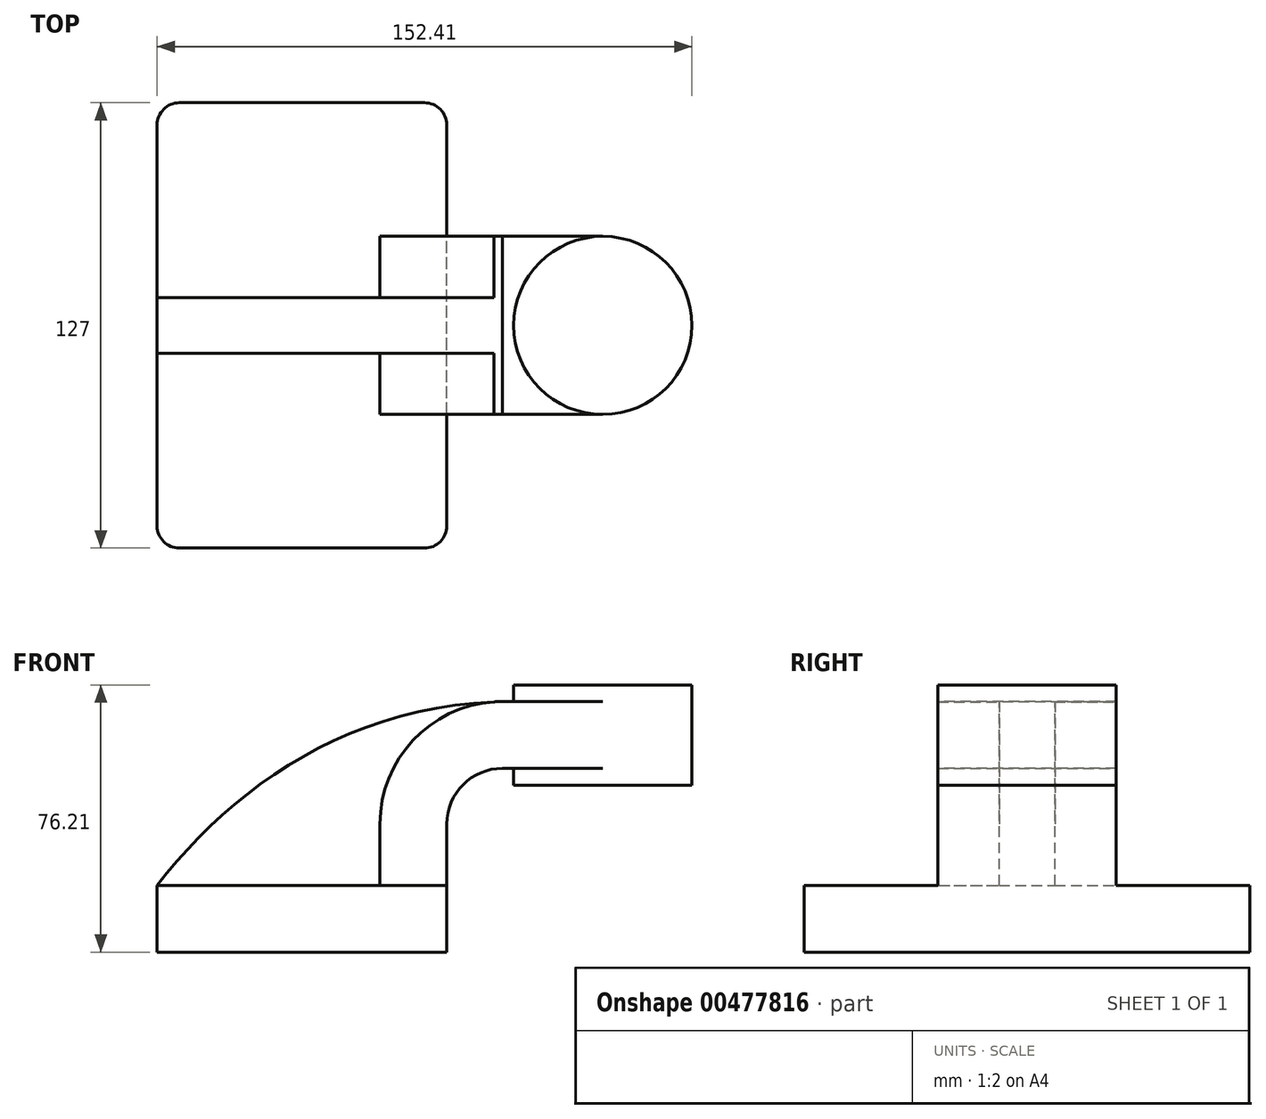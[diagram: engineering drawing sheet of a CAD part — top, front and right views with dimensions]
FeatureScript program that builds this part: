
annotation { "Feature Type Name" : "Feature", "Feature Type Description" : "" }
export const myFeature = defineFeature(function(context is Context, id is Id, definition is map)
    precondition{}
    {
        {
            var Q0;
            Q0=qCreatedBy(makeId("Front.planeOp"),FACE);
            var sketch = newSketch(context, id + "F0", { "sketchPlane" : qUnion([Q0])});
            skLineSegment(sketch, "E0.bottom", {"start": v(41.27, 9.53) * mm, "end": v(-41.27, 9.53) * mm});
            skLineSegment(sketch, "E0.top", {"start": v(41.28, -9.52) * mm, "end": v(-41.27, -9.52) * mm});
            skLineSegment(sketch, "E0.left", {"start": v(41.28, 9.53) * mm, "end": v(41.28, -9.52) * mm});
            skLineSegment(sketch, "E0.right", {"start": v(-41.27, 9.53) * mm, "end": v(-41.27, -9.52) * mm});
            skPoint(sketch, "E0.middle", {"position": v(0, 0) * mm});
            skLineSegment(sketch, "E1.bottom", {"start": v(60.32, 38.1) * mm, "end": v(111.12, 38.1) * mm});
            skLineSegment(sketch, "E1.top", {"start": v(60.32, 66.68) * mm, "end": v(111.12, 66.68) * mm});
            skLineSegment(sketch, "E1.left", {"start": v(60.32, 38.1) * mm, "end": v(60.32, 66.68) * mm});
            skLineSegment(sketch, "E1.right", {"start": v(111.12, 38.1) * mm, "end": v(111.12, 66.68) * mm});
            skPoint(sketch, "E1.middle", {"position": v(85.72, 52.39) * mm});
            skLineSegment(sketch, "E2", {"start": v(41.27, 9.53) * mm, "end": v(41.27, 27) * mm});
            skArc(sketch, "E3", {"start": v(41.27, 27) * mm, "mid": v(45.92, 38.23) * mm, "end": v(57.15, 42.88) * mm});
            skLineSegment(sketch, "E4", {"start": v(57.15, 42.88) * mm, "end": v(85.72, 42.88) * mm});
            skLineSegment(sketch, "E5.0", {"start": v(57.15, 61.93) * mm, "end": v(85.72, 61.93) * mm});
            skArc(sketch, "E5.1", {"start": v(22.22, 27) * mm, "mid": v(32.45, 51.7) * mm, "end": v(57.15, 61.93) * mm});
            skLineSegment(sketch, "E5.2", {"start": v(22.22, 9.53) * mm, "end": v(22.22, 27) * mm});
            skFitSpline(sketch, "E6", {"points": [v(-41.27, 9.53) * mm, v(57.15, 61.93) * mm], "startDerivative": vector(63.52, 81.79) * mm, "endDerivative": vector(134.24, 3.46) * mm});
            skLineSegment(sketch, "E7", {"start": v(85.72, 66.68) * mm, "end": v(85.72, 38.1) * mm});
            skSolve(sketch);
        }
        {
            var Q0;
            Q0=makeQuery(id+"F0.imprint","IMPRINT",FACE,{"disambiguationData":[TD([[makeQuery(id+"F0.imprint","IMPRINT",EDGE,{"derivedFrom":sQuery(id+"F0.wireOp",EDGE,"E0.top")}),-1.0]])]});
            extrude(context, id + "F1", {"entities" : qUnion([Q0]), "endBound" : BoundingType.SYMMETRIC, "depth" : 127 * mm});
        }
        {
            var Q0;
            {var subQ1=sQuery(id+"F0.wireOp",EDGE,"E2");Q0=makeQuery(id+"F0.imprint","IMPRINT",FACE,{"disambiguationData":[TD([[makeQuery(id+"F0.imprint","IMPRINT",EDGE,{"derivedFrom":subQ1}),1.0]])]});}
            var Q1;
            {var subQ0=sQuery(id+"F0.wireOp",EDGE,"E4");var subQ1=sQuery(id+"F0.wireOp",EDGE,"E1.left");var subQ2=makeQuery(id+"F0.imprint","INTERSECT",VERTEX,{"derivedFrom":[subQ1,subQ0]});Q1=makeQuery(id+"F0.imprint","IMPRINT",FACE,{"disambiguationData":[TD([[makeQuery(id+"F0.imprint","IMPRINT",EDGE,{"disambiguationData":[TD([[subQ2,-1.0]])],"derivedFrom":subQ1}),-1.0]])]});}
            extrude(context, id + "F2", {"entities" : qUnion([Q0, Q1]), "operationType" : NewBodyOperationType.ADD, "endBound" : BoundingType.SYMMETRIC, "depth" : 50.8 * mm});
        }
        {
            var Q0;
            {var subQ3=sQuery(id+"F0.wireOp",EDGE,"E5.2");Q0=makeQuery(id+"F0.imprint","IMPRINT",FACE,{"disambiguationData":[TD([[makeQuery(id+"F0.imprint","IMPRINT",EDGE,{"derivedFrom":subQ3}),1.0]])]});}
            extrude(context, id + "F3", {"entities" : qUnion([Q0]), "operationType" : NewBodyOperationType.ADD, "endBound" : BoundingType.SYMMETRIC, "depth" : 15.88 * mm});
        }
        {
            var Q0;
            {var subQ4=sQuery(id+"F0.wireOp",EDGE,"E1.right");Q0=makeQuery(id+"F0.imprint","IMPRINT",FACE,{"disambiguationData":[TD([[makeQuery(id+"F0.imprint","IMPRINT",EDGE,{"derivedFrom":subQ4}),1.0]])]});}
            var Q1;
            Q1=sQuery(id+"F0.wireOp",EDGE,"E7");
            revolve(context, id + "F4", {"operationType" : NewBodyOperationType.ADD, "entities" : qUnion([Q0]), "axis" : qUnion([Q1]), "revolveType" : RevolveType.FULL});
        }
        {
            var Q0;
            Q0=makeQuery(id+"F1.opExtrude","CAP_EDGE",EDGE,{"disambiguationData":[OSD([sQuery(id+"F0.wireOp",EDGE,"E0.left")])],"isStart":false});
            var Q1;
            Q1=makeQuery(id+"F1.opExtrude","CAP_EDGE",EDGE,{"disambiguationData":[OSD([sQuery(id+"F0.wireOp",EDGE,"E0.right")])],"isStart":false});
            var Q2;
            Q2=makeQuery(id+"F1.opExtrude","CAP_EDGE",EDGE,{"disambiguationData":[OSD([sQuery(id+"F0.wireOp",EDGE,"E0.right")])],"isStart":true});
            var Q3;
            Q3=makeQuery(id+"F1.opExtrude","CAP_EDGE",EDGE,{"disambiguationData":[OSD([sQuery(id+"F0.wireOp",EDGE,"E0.left")])],"isStart":true});
            fillet(context, id + "F5", {"entities" : qUnion([Q0, Q1, Q2, Q3]), "radius" : 6.35 * mm, "tangentPropagation" : true, "allowEdgeOverflow" : false});
        }
    });
